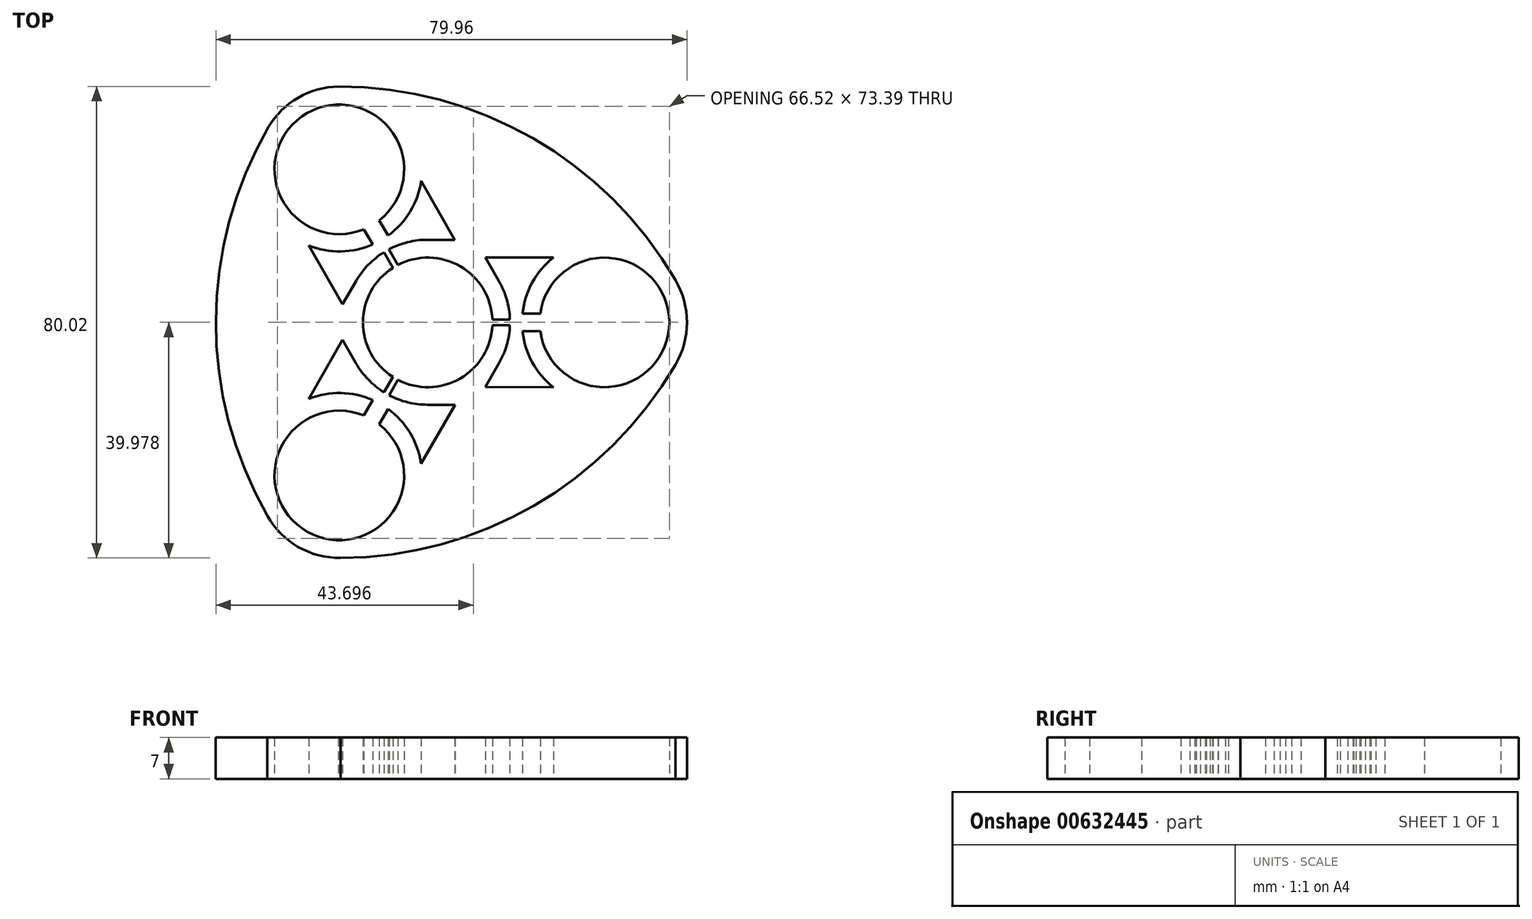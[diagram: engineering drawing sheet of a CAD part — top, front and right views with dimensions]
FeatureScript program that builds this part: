
annotation { "Feature Type Name" : "Feature", "Feature Type Description" : "" }
export const myFeature = defineFeature(function(context is Context, id is Id, definition is map)
    precondition{}
    {
        {
            var Q0;
            Q0=qCreatedBy(makeId("Top.planeOp"),FACE);
            var sketch = newSketch(context, id + "F0", { "sketchPlane" : qUnion([Q0])});
            skArc(sketch, "E0", {"start": v(37.99, 28.11) * mm, "mid": v(32.92, 18.85) * mm, "end": v(37.99, 9.58) * mm});
            skArc(sketch, "E1.1.0.0", {"start": v(65.26, 29.85) * mm, "mid": v(61.67, 25.63) * mm, "end": v(60, 20.35) * mm});
            skArc(sketch, "E1.1.0.1", {"start": v(63.02, 17.35) * mm, "mid": v(84.92, 18.85) * mm, "end": v(63.02, 20.35) * mm});
            skLineSegment(sketch, "E1.direction1", {"start": v(43.92, 18.85) * mm, "end": v(73.92, 18.85) * mm, "construction": true});
            skArc(sketch, "E2.1.0", {"start": v(35.66, 36.14) * mm, "mid": v(23.42, 54.35) * mm, "end": v(33.07, 34.64) * mm});
            skArc(sketch, "E2.2.0", {"start": v(33.07, 3.05) * mm, "mid": v(23.42, -16.66) * mm, "end": v(35.66, 1.55) * mm});
            skArc(sketch, "E3", {"start": v(16.69, -13.95) * mm, "mid": v(7.96, 19.06) * mm, "end": v(16.9, 52.01) * mm});
            skLineSegment(sketch, "E4", {"start": v(60, 20.35) * mm, "end": v(63.02, 20.35) * mm});
            skLineSegment(sketch, "E5.trimOffspring", {"start": v(60, 17.35) * mm, "end": v(63.02, 17.35) * mm});
            skLineSegment(sketch, "E6.0", {"start": v(43.92, 18.35) * mm, "end": v(44.2, 18.35) * mm});
            skLineSegment(sketch, "E7.0", {"start": v(43.92, 19.35) * mm, "end": v(44.2, 19.35) * mm});
            skLineSegment(sketch, "E8.1.2", {"start": v(37.21, 33.58) * mm, "end": v(35.66, 36.14) * mm});
            skLineSegment(sketch, "E8.1.3", {"start": v(34.61, 32.08) * mm, "end": v(33.07, 34.64) * mm});
            skLineSegment(sketch, "E8.1.6", {"start": v(44.35, 19.1) * mm, "end": v(44.2, 19.35) * mm});
            skLineSegment(sketch, "E8.1.7", {"start": v(43.48, 18.6) * mm, "end": v(43.34, 18.85) * mm});
            skArc(sketch, "E8.1.9", {"start": v(85.93, 11.67) * mm, "mid": v(61.9, -12.3) * mm, "end": v(29.13, -21.13) * mm});
            skLineSegment(sketch, "E8.2.2", {"start": v(34.58, 5.67) * mm, "end": v(33.07, 3.05) * mm});
            skLineSegment(sketch, "E8.2.3", {"start": v(37.18, 4.17) * mm, "end": v(35.66, 1.55) * mm});
            skLineSegment(sketch, "E8.2.6", {"start": v(43.48, 19.1) * mm, "end": v(43.34, 18.85) * mm});
            skLineSegment(sketch, "E8.2.7", {"start": v(44.35, 18.6) * mm, "end": v(44.2, 18.35) * mm});
            skArc(sketch, "E8.2.9", {"start": v(28.78, 58.89) * mm, "mid": v(61.76, 50.11) * mm, "end": v(85.93, 26.03) * mm});
            skArc(sketch, "E9.trimOffspring", {"start": v(23.72, 31.9) * mm, "mid": v(29.18, 30.9) * mm, "end": v(34.61, 32.08) * mm});
            skLineSegment(sketch, "E10.trimOffspring", {"start": v(37.99, 28.11) * mm, "end": v(36.47, 30.75) * mm});
            skLineSegment(sketch, "E11.trimOffspring", {"start": v(38.86, 28.61) * mm, "end": v(37.33, 31.25) * mm});
            skLineSegment(sketch, "E12.trimOffspring", {"start": v(31.78, 25.93) * mm, "end": v(29.48, 21.92) * mm});
            skLineSegment(sketch, "E13.trimOffspring", {"start": v(29.44, 15.87) * mm, "end": v(23.72, 5.87) * mm});
            skLineSegment(sketch, "E14.trimOffspring", {"start": v(43.87, 32.87) * mm, "end": v(48.5, 32.87) * mm});
            skArc(sketch, "E15.trimOffspring", {"start": v(31.75, 11.87) * mm, "mid": v(33.82, 9.14) * mm, "end": v(36.49, 6.98) * mm});
            skLineSegment(sketch, "E16.trimOffspring", {"start": v(29.48, 21.92) * mm, "end": v(23.72, 31.9) * mm});
            skArc(sketch, "E17.trimOffspring", {"start": v(37.21, 33.58) * mm, "mid": v(40.95, 37.67) * mm, "end": v(42.8, 42.89) * mm});
            skArc(sketch, "E18.trimOffspring", {"start": v(36.47, 30.75) * mm, "mid": v(33.83, 28.63) * mm, "end": v(31.78, 25.93) * mm});
            skArc(sketch, "E19.trimOffspring", {"start": v(28.78, 58.89) * mm, "mid": v(21.94, 57) * mm, "end": v(16.9, 52.01) * mm});
            skArc(sketch, "E20.trimOffspring", {"start": v(43.87, 32.87) * mm, "mid": v(40.5, 32.46) * mm, "end": v(37.33, 31.25) * mm});
            skLineSegment(sketch, "E21.trimOffspring", {"start": v(48.5, 32.87) * mm, "end": v(42.8, 42.89) * mm});
            skLineSegment(sketch, "E22.trimOffspring", {"start": v(53.69, 29.87) * mm, "end": v(65.26, 29.85) * mm});
            skLineSegment(sketch, "E23.trimOffspring", {"start": v(56, 11.87) * mm, "end": v(53.7, 7.87) * mm});
            skLineSegment(sketch, "E24.trimOffspring", {"start": v(48.54, 4.85) * mm, "end": v(42.77, -5.13) * mm});
            skLineSegment(sketch, "E25.trimOffspring", {"start": v(54.9, 19.35) * mm, "end": v(57.87, 19.35) * mm});
            skLineSegment(sketch, "E26.trimOffspring", {"start": v(54.9, 18.35) * mm, "end": v(57.86, 18.35) * mm});
            skLineSegment(sketch, "E27.trimOffspring", {"start": v(56, 25.87) * mm, "end": v(53.69, 29.87) * mm});
            skArc(sketch, "E28.trimOffspring", {"start": v(54.9, 19.35) * mm, "mid": v(49.42, 28.37) * mm, "end": v(38.86, 28.61) * mm});
            skArc(sketch, "E29.trimOffspring", {"start": v(57.87, 19.35) * mm, "mid": v(57.33, 22.73) * mm, "end": v(56, 25.87) * mm});
            skArc(sketch, "E30.trimOffspring", {"start": v(60, 17.35) * mm, "mid": v(61.67, 12.07) * mm, "end": v(65.26, 7.85) * mm});
            skArc(sketch, "E31.trimOffspring", {"start": v(85.93, 11.67) * mm, "mid": v(87.92, 18.85) * mm, "end": v(85.93, 26.03) * mm});
            skLineSegment(sketch, "E32.trimOffspring", {"start": v(31.75, 11.87) * mm, "end": v(29.44, 15.87) * mm});
            skArc(sketch, "E33.trimOffspring", {"start": v(16.69, -13.95) * mm, "mid": v(21.92, -19.26) * mm, "end": v(29.13, -21.13) * mm});
            skArc(sketch, "E34.trimOffspring", {"start": v(42.77, -5.13) * mm, "mid": v(40.91, 0.08) * mm, "end": v(37.18, 4.17) * mm});
            skLineSegment(sketch, "E35.trimOffspring", {"start": v(38.86, 9.08) * mm, "end": v(37.36, 6.48) * mm});
            skLineSegment(sketch, "E36.trimOffspring", {"start": v(37.99, 9.58) * mm, "end": v(36.49, 6.98) * mm});
            skArc(sketch, "E37.trimOffspring", {"start": v(56, 11.87) * mm, "mid": v(57.33, 15) * mm, "end": v(57.86, 18.35) * mm});
            skArc(sketch, "E38.trimOffspring", {"start": v(38.86, 9.08) * mm, "mid": v(49.42, 9.32) * mm, "end": v(54.9, 18.35) * mm});
            skLineSegment(sketch, "E39.trimOffspring", {"start": v(53.7, 7.87) * mm, "end": v(65.26, 7.85) * mm});
            skLineSegment(sketch, "E40.trimOffspring", {"start": v(43.87, 4.87) * mm, "end": v(48.54, 4.85) * mm});
            skArc(sketch, "E41.trimOffspring", {"start": v(37.36, 6.48) * mm, "mid": v(40.52, 5.28) * mm, "end": v(43.87, 4.87) * mm});
            skArc(sketch, "E42.trimOffspring", {"start": v(34.58, 5.67) * mm, "mid": v(29.17, 6.86) * mm, "end": v(23.72, 5.87) * mm});
            skLineSegment(sketch, "E43", {"start": v(43.92, 18.85) * mm, "end": v(-2.93, 18.85) * mm});
            skPoint(sketch, "E43.endSnap0", {"position": v(7.96, 18.85) * mm});
            skSolve(sketch);
        }
        {
            var Q0;
            Q0=makeQuery(id+"F0.imprint","IMPRINT",FACE,{"disambiguationData":[TD([[makeQuery(id+"F0.imprint","IMPRINT",EDGE,{"derivedFrom":sQuery(id+"F0.wireOp",EDGE,"E0")}),-1.0]])]});
            extrude(context, id + "F1", {"entities" : qUnion([Q0]), "depth" : 7 * mm, "offsetDistance" : 25 * mm});
        }
    });
